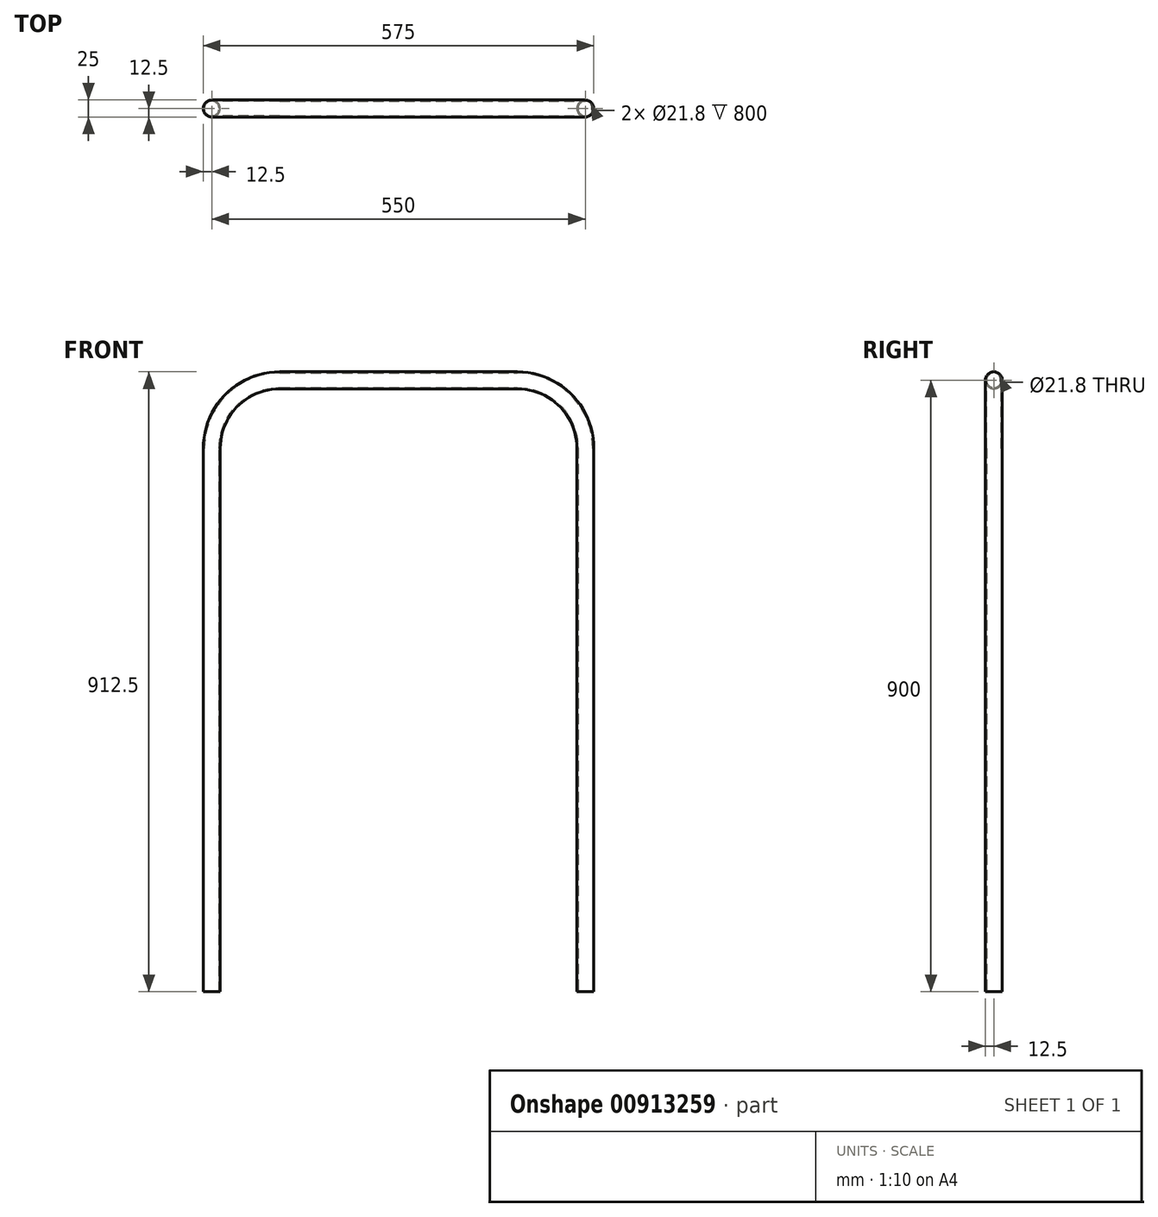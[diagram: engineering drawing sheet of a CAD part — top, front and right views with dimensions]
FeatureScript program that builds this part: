
annotation { "Feature Type Name" : "Feature", "Feature Type Description" : "" }
export const myFeature = defineFeature(function(context is Context, id is Id, definition is map)
    precondition{}
    {
        {
            var Q0;
            Q0=qCreatedBy(makeId("Top.planeOp"),FACE);
            var sketch = newSketch(context, id + "F0", { "sketchPlane" : qUnion([Q0])});
            skCircle(sketch, "E0", {"center": v(0, 0) * mm, "radius": 12.5 * mm});
            skCircle(sketch, "E1", {"center": v(0, 0) * mm, "radius": 10.9 * mm});
            skSolve(sketch);
        }
        {
            var Q0;
            Q0=qCreatedBy(makeId("Front.planeOp"),FACE);
            var sketch = newSketch(context, id + "F1", { "sketchPlane" : qUnion([Q0])});
            skLineSegment(sketch, "E2.top", {"start": v(100, 900) * mm, "end": v(450, 900) * mm});
            skLineSegment(sketch, "E2.left", {"start": v(0, 0) * mm, "end": v(0, 800) * mm});
            skLineSegment(sketch, "E2.right", {"start": v(550, 0) * mm, "end": v(550, 800) * mm});
            skPoint(sketch, "E3.visualSharp", {"position": v(550, 900) * mm});
            skArc(sketch, "E3.filletArc", {"start": v(550, 800) * mm, "mid": v(520.71, 870.71) * mm, "end": v(450, 900) * mm});
            skPoint(sketch, "E4.visualSharp", {"position": v(0, 900) * mm});
            skArc(sketch, "E4.filletArc", {"start": v(100, 900) * mm, "mid": v(29.29, 870.71) * mm, "end": v(0, 800) * mm});
            skSolve(sketch);
        }
        {
            var Q0;
            Q0=makeQuery(id+"F0.imprint","IMPRINT",FACE,{"disambiguationData":[TD([[makeQuery(id+"F0.imprint","IMPRINT",EDGE,{"derivedFrom":sQuery(id+"F0.wireOp",EDGE,"E0")}),1.0]])]});
            var Q1;
            Q1=sQuery(id+"F1.wireOp",EDGE,"E2.left");
            var Q2;
            Q2=sQuery(id+"F1.wireOp",EDGE,"E4.filletArc");
            var Q3;
            Q3=sQuery(id+"F1.wireOp",EDGE,"E2.top");
            var Q4;
            Q4=sQuery(id+"F1.wireOp",EDGE,"E3.filletArc");
            var Q5;
            Q5=sQuery(id+"F1.wireOp",EDGE,"E2.right");
            sweep(context, id + "F2", {"profiles" : qUnion([Q0]), "path" : qUnion([Q1, Q2, Q3, Q4, Q5])});
        }
    });
